# Revit family: TR2003
name_source: partatom
category: Verbindungsmittel
units: mm (PartAtom-declared; Revit-internal decimal feet)

## family parameters
Arbeitsebenenbasiert = Nein
Beim Laden mit Abzugskörper schneiden = Nein
Gemeinsam genutzt = Nein
Immer vertikal = Nein
OmniClass-Nummer = 23.25.10.27.11.21
OmniClass-Titel = Reinforcement Couplers

## types (10) — shared parameters
Endenbearbeitung 1 = Mit Gewinde
Endenbearbeitung 2 = Mit Gewinde
Hersteller = Stahlwerk Annahütte Max Aicher GmbH Co.KG
Modell = TR 2003
Stabgröße 2 = Keine
TR2003-G_Vis = Ja
TR2003-L_Vis = Ja
TR2003-SW_Vis = Ja
Typenbild = TR2003.png
Typenkommentare = TR 2003 - Kontermutter, lang
URL = http//:www.annahuette.com
zero-valued in all types: Einfassung Stab 2

## per-type parameters (varying)
| type | Außendurchmesser | Beschreibung | Einfassung Stab 1 | Gesamtlänge | Körper | Stabgröße 1 | TR2003-G | TR2003-L | TR2003-SW | TR2003-ød |
| TR 2003-ø18 | 30 mm  [stored 0.0984252 ft] | TR2003-ø18 | 40 mm  [stored 0.131234 ft] | 40 mm  [stored 0.131234 ft] | 0,16 kg | SAS 670 - ø18 | 0,16 kg | 40 mm  [stored 0.131234 ft] | 30 mm  [stored 0.0984252 ft] | 18 mm  [stored 0.0590551 ft] |
| TR 2003-ø22 | 36 mm  [stored 0.11811 ft] | TR2003-ø22 | 45 mm  [stored 0.147638 ft] | 45 mm  [stored 0.147638 ft] | 0,25 kg | SAS 670 - ø22 | 0,25 kg | 45 mm  [stored 0.147638 ft] | 36 mm  [stored 0.11811 ft] | 22 mm  [stored 0.0721785 ft] |
| TR 2003-ø25 | 41 mm  [stored 0.134514 ft] | TR2003-ø25 | 50 mm  [stored 0.164042 ft] | 50 mm  [stored 0.164042 ft] | 0,37 kg | SAS 670 - ø25 | 0,37 kg | 50 mm  [stored 0.164042 ft] | 41 mm  [stored 0.134514 ft] | 25 mm  [stored 0.082021 ft] |
| TR 2003-ø28 | 46 mm  [stored 0.150919 ft] | TR2003-ø28 | 55 mm  [stored 0.180446 ft] | 55 mm  [stored 0.180446 ft] | 0,50 kg | SAS 670 - ø28 | 0,50 kg | 55 mm  [stored 0.180446 ft] | 46 mm  [stored 0.150919 ft] | 28 mm  [stored 0.0918635 ft] |
| TR 2003-ø30 | 50 mm  [stored 0.164042 ft] | TR2003-ø30 | 60 mm  [stored 0.19685 ft] | 60 mm  [stored 0.19685 ft] | 0,67 kg | SAS 670 - ø30 | 0,67 kg | 60 mm  [stored 0.19685 ft] | 50 mm  [stored 0.164042 ft] | 30 mm  [stored 0.0984252 ft] |
| TR 2003-ø35 | 55 mm  [stored 0.180446 ft] | TR2003-ø35 | 65 mm  [stored 0.213255 ft] | 65 mm  [stored 0.213255 ft] | 0,78 kg | SAS 670 - ø35 | 0,78 kg | 65 mm  [stored 0.213255 ft] | 55 mm  [stored 0.180446 ft] | 35 mm  [stored 0.114829 ft] |
| TR 2003-ø43 | 70 mm  [stored 0.229659 ft] | TR2003-ø43 | 80 mm  [stored 0.262467 ft] | 80 mm  [stored 0.262467 ft] | 1,60 kg | SAS 670 - ø43 | 1,60 kg | 80 mm  [stored 0.262467 ft] | 70 mm  [stored 0.229659 ft] | 43 mm  [stored 0.141076 ft] |
| TR 2003-ø50 | 80 mm  [stored 0.262467 ft] | TR2003-ø50 | 90 mm  [stored 0.295276 ft] | 90 mm  [stored 0.295276 ft] | 2,27 kg | SAS 670 - ø50 | 2,27 kg | 90 mm  [stored 0.295276 ft] | 80 mm  [stored 0.262467 ft] | 50 mm  [stored 0.164042 ft] |
| TR 2003-ø57,5 | 90 mm  [stored 0.295276 ft] | TR2003-ø57,5 | 100 mm  [stored 0.328084 ft] | 100 mm  [stored 0.328084 ft] | 3,71 kg | SAS 670 - ø57,5 | 3,71 kg | 100 mm  [stored 0.328084 ft] | 90 mm  [stored 0.295276 ft] | 58 mm |
| TR 2003-ø63,5 | 100 mm  [stored 0.328084 ft] | TR2003-ø63,5 | 115 mm  [stored 0.377297 ft] | 115 mm  [stored 0.377297 ft] | 5,45 kg | SAS 670 - ø63,5 | 5,45 kg | 115 mm  [stored 0.377297 ft] | 100 mm  [stored 0.328084 ft] | 64 mm |

note: [stored X ft] marks values corroborated as IEEE doubles in the binary element streams (Revit-internal decimal feet)
